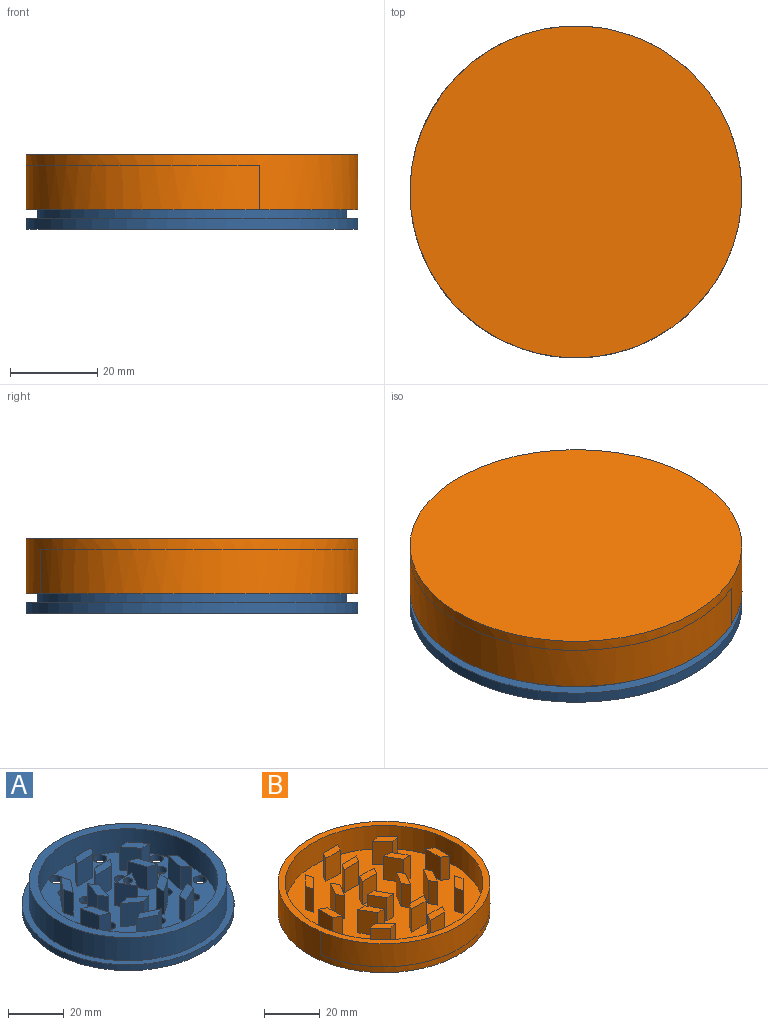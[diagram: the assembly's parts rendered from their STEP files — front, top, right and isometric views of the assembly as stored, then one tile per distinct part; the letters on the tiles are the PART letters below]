
ASSEMBLY  parts=2 mates=1
PART A: 94 faces, bbox 76.2x76.2x12.7 mm
  f0: plane 64.46x64.46mm, normal (0,0,1), area 2540.7mm2, adj f6,f7,f9,f12,f13,f14,f15,f17
  f1: cylinder r=38.1mm len=76.2mm, axis (0,0,1), area 608mm2, adj f2,f3
  f2: plane 76.2x76.2mm, normal (0,0,-1), area 4189.6mm2, adj f1,f72,f73,f74,f75,f76,f77,f78
  f3: plane 76.2x76.2mm, normal (0,0,1), area 587.8mm2, adj f1,f4
  f4: cylinder r=35.56mm len=71.12mm, axis (0,0,-1), area 2270mm2, adj f3,f5
  f5: plane 71.12x71.12mm, normal (0,0,1), area 709.6mm2, adj f4,f93
  f6: plane 10.16x8.42mm, normal (0,1,0), area 85.6mm2, adj f0,f7,f9,f10
  f7: plane 10.16x7.29mm, normal (-0.87,-0.5,0), area 85.6mm2, adj f0,f6,f9,f10
  f8: cylinder r=1.65mm len=10.16mm, axis (0,0,-1), area 105.4mm2, adj f10,f11
  f9: plane 10.16x7.29mm, normal (0.87,-0.5,0), area 85.6mm2, adj f0,f6,f7,f10
  f10: plane 8.42x7.29mm, normal (0,0,1), area 22.1mm2, adj f6,f7,f8,f9
  f11: plane 3.3x3.3mm, normal (0,0,1), area 8.6mm2, adj f8
  f12: plane 10.16x8.08mm, normal (0,-1,0), area 82.1mm2, adj f0,f13,f15,f16
  f13: plane 10.16x3.25mm, normal (0.8,-0.6,0), area 41.4mm2, adj f0,f12,f14,f16
  f14: plane 10.16x8.08mm, normal (0,1,0), area 82.1mm2, adj f0,f13,f15,f16
  f15: plane 10.16x3.25mm, normal (-0.8,0.6,0), area 41.4mm2, adj f0,f12,f14,f16
  f16: plane 10.53x3.25mm, normal (0,0,1), area 26.3mm2, adj f12,f13,f14,f15
  f17: plane 10.16x7.68mm, normal (-0.95,0.31,0), area 82.1mm2, adj f0,f18,f20,f21
  f18: plane 10.16x3.34mm, normal (-0.82,-0.57,0), area 41.4mm2, adj f0,f17,f19,f21
  f19: plane 10.16x7.68mm, normal (0.95,-0.31,0), area 82.1mm2, adj f0,f18,f20,f21
  f20: plane 10.16x3.34mm, normal (0.82,0.57,0), area 41.4mm2, adj f0,f17,f19,f21
  f21: plane 11.02x4.83mm, normal (0,0,1), area 26.3mm2, adj f17,f18,f19,f20
  f22: plane 10.16x6.53mm, normal (-0.59,-0.81,0), area 82.1mm2, adj f0,f23,f25,f26
  f23: plane 10.16x3.9mm, normal (0.29,-0.96,0), area 41.4mm2, adj f0,f22,f24,f26
  f24: plane 10.16x6.53mm, normal (0.59,0.81,0), area 82.1mm2, adj f0,f23,f25,f26
  f25: plane 10.16x3.9mm, normal (-0.29,0.96,0), area 41.4mm2, adj f0,f22,f24,f26
  f26: plane 10.43x5.94mm, normal (0,0,1), area 26.3mm2, adj f22,f23,f24,f25
  f27: plane 10.16x6.53mm, normal (0.59,-0.81,0), area 82.1mm2, adj f0,f28,f30,f31
  f28: plane 10.16x4.07mm, normal (1,-0.02,0), area 41.4mm2, adj f0,f27,f29,f31
  f29: plane 10.16x6.53mm, normal (-0.59,0.81,0), area 82.1mm2, adj f0,f28,f30,f31
  f30: plane 10.16x4.07mm, normal (-1,0.02,0), area 41.4mm2, adj f0,f27,f29,f31
  f31: plane 8.82x6.61mm, normal (0,0,1), area 26.3mm2, adj f27,f28,f29,f30
  f32: plane 10.16x7.68mm, normal (0.95,0.31,0), area 82.1mm2, adj f0,f33,f35,f36
  f33: plane 10.16x3.85mm, normal (0.33,0.95,0), area 41.4mm2, adj f0,f32,f34,f36
  f34: plane 10.16x7.68mm, normal (-0.95,-0.31,0), area 82.1mm2, adj f0,f33,f35,f36
  f35: plane 10.16x3.85mm, normal (-0.33,-0.95,0), area 41.4mm2, adj f0,f32,f34,f36
  f36: plane 9.01x6.35mm, normal (0,0,1), area 26.3mm2, adj f32,f33,f34,f35
  f37: plane 10.16x8.08mm, normal (0,-1,0), area 82.1mm2, adj f0,f38,f40,f41
  f38: plane 10.16x3.35mm, normal (0.8,-0.59,0), area 42.3mm2, adj f0,f37,f39,f41
  f39: plane 10.16x8.08mm, normal (0,1,0), area 82.1mm2, adj f0,f38,f40,f41
  f40: plane 10.16x3.35mm, normal (-0.8,0.59,0), area 42.3mm2, adj f0,f37,f39,f41
  f41: plane 10.55x3.35mm, normal (0,0,1), area 27.1mm2, adj f37,f38,f39,f40
  f42: plane 10.16x4.02mm, normal (-0.97,-0.26,0), area 42.3mm2, adj f0,f43,f45,f46
  f43: plane 10.16x6.31mm, normal (0.78,-0.62,0), area 82.1mm2, adj f0,f42,f44,f46
  f44: plane 10.16x4.02mm, normal (0.97,0.26,0), area 42.3mm2, adj f0,f43,f45,f46
  f45: plane 10.16x6.31mm, normal (-0.78,0.62,0), area 82.1mm2, adj f0,f42,f44,f46
  f46: plane 10.34x6.11mm, normal (0,0,1), area 27.1mm2, adj f42,f43,f44,f45
  f47: plane 10.16x3.82mm, normal (-0.4,-0.92,0), area 42.3mm2, adj f0,f48,f50,f51
  f48: plane 10.16x7.87mm, normal (0.97,0.22,0), area 82.1mm2, adj f0,f47,f49,f51
  f49: plane 10.16x3.82mm, normal (0.4,0.92,0), area 42.3mm2, adj f0,f48,f50,f51
  f50: plane 10.16x7.87mm, normal (-0.97,-0.22,0), area 82.1mm2, adj f0,f47,f49,f51
  f51: plane 9.54x5.61mm, normal (0,0,1), area 27.1mm2, adj f47,f48,f49,f50
  f52: plane 10.16x3.68mm, normal (0.47,-0.88,0), area 42.3mm2, adj f0,f53,f55,f56
  f53: plane 10.16x7.28mm, normal (0.43,0.9,0), area 82.1mm2, adj f0,f52,f54,f56
  f54: plane 10.16x3.68mm, normal (-0.47,0.88,0), area 42.3mm2, adj f0,f53,f55,f56
  f55: plane 10.16x7.28mm, normal (-0.43,-0.9,0), area 82.1mm2, adj f0,f52,f54,f56
  f56: plane 10.96x5.45mm, normal (0,0,1), area 27.1mm2, adj f52,f53,f54,f55
  f57: plane 10.16x4.09mm, normal (0.98,-0.19,0), area 42.3mm2, adj f0,f58,f60,f61
  f58: plane 10.16x7.28mm, normal (-0.43,0.9,0), area 82.1mm2, adj f0,f57,f59,f61
  f59: plane 10.16x4.09mm, normal (-0.98,0.19,0), area 42.3mm2, adj f0,f58,f60,f61
  f60: plane 10.16x7.28mm, normal (0.43,-0.9,0), area 82.1mm2, adj f0,f57,f59,f61
  f61: plane 8.05x7.6mm, normal (0,0,1), area 27.1mm2, adj f57,f58,f59,f60
  f62: plane 10.16x3.16mm, normal (0.76,0.65,0), area 42.3mm2, adj f0,f63,f65,f66
  f63: plane 10.16x7.87mm, normal (-0.97,0.22,0), area 82.1mm2, adj f0,f62,f64,f66
  f64: plane 10.16x3.16mm, normal (-0.76,-0.65,0), area 42.3mm2, adj f0,f63,f65,f66
  f65: plane 10.16x7.87mm, normal (0.97,-0.22,0), area 82.1mm2, adj f0,f62,f64,f66
  f66: plane 11.03x4.51mm, normal (0,0,1), area 27.1mm2, adj f62,f63,f64,f65
  f67: plane 10.16x4.16mm, normal (-0.04,1,0), area 42.3mm2, adj f0,f68,f70,f71
  f68: plane 10.16x6.31mm, normal (-0.78,-0.62,0), area 82.1mm2, adj f0,f67,f69,f71
  f69: plane 10.16x4.16mm, normal (0.04,-1,0), area 42.3mm2, adj f0,f68,f70,f71
  f70: plane 10.16x6.31mm, normal (0.78,0.62,0), area 82.1mm2, adj f0,f67,f69,f71
  f71: plane 9.2x6.47mm, normal (0,0,1), area 27.1mm2, adj f67,f68,f69,f70
  f72: cylinder r=2.44mm len=4.88mm, axis (0,0,1), area 38.9mm2, adj f0,f2
  f73: cylinder r=2.31mm len=4.62mm, axis (0,0,1), area 36.9mm2, adj f0,f2
  f74: cylinder r=2.31mm len=4.62mm, axis (0,0,1), area 36.9mm2, adj f0,f2
  f75: cylinder r=2.31mm len=4.62mm, axis (0,0,1), area 36.9mm2, adj f0,f2
  f76: cylinder r=2.31mm len=4.62mm, axis (0,0,1), area 36.9mm2, adj f0,f2
  f77: cylinder r=2.44mm len=4.88mm, axis (0,0,1), area 38.9mm2, adj f0,f2
  f78: cylinder r=2.44mm len=4.88mm, axis (0,0,1), area 38.9mm2, adj f0,f2
  f79: cylinder r=2.44mm len=4.88mm, axis (0,0,1), area 38.9mm2, adj f0,f2
  f80: cylinder r=2.44mm len=4.88mm, axis (0,0,1), area 38.9mm2, adj f0,f2
  f81: cylinder r=2.44mm len=4.88mm, axis (0,0,1), area 38.9mm2, adj f0,f2
  f82: cylinder r=2.44mm len=4.88mm, axis (0,0,1), area 38.9mm2, adj f0,f2
  f83: cylinder r=2.44mm len=4.88mm, axis (0,0,1), area 38.9mm2, adj f0,f2
  f84: cylinder r=2.44mm len=4.88mm, axis (0,0,1), area 38.9mm2, adj f0,f2
  f85: cylinder r=2.31mm len=4.62mm, axis (0,0,1), area 36.9mm2, adj f0,f2
  f86: cylinder r=2.33mm len=4.65mm, axis (0,0,1), area 37.1mm2, adj f0,f2
  f87: cylinder r=2.33mm len=4.65mm, axis (0,0,1), area 37.1mm2, adj f0,f2
  f88: cylinder r=2.33mm len=4.65mm, axis (0,0,1), area 37.1mm2, adj f0,f2
  f89: cylinder r=2.33mm len=4.65mm, axis (0,0,1), area 37.1mm2, adj f0,f2
  f90: cylinder r=2.33mm len=4.65mm, axis (0,0,1), area 37.1mm2, adj f0,f2
  f91: cylinder r=2.33mm len=4.65mm, axis (0,0,1), area 37.1mm2, adj f0,f2
  f92: cylinder r=2.33mm len=4.65mm, axis (0,0,1), area 37.1mm2, adj f0,f2
  f93: cylinder r=32.23mm len=64.46mm, axis (0,0,-1), area 2057.3mm2, adj f0,f5
PART B: 91 faces, bbox 76.2x76.2x12.7 mm
  f0: plane 71.12x71.12mm, normal (0,0,1), area 3599.7mm2, adj f4,f6,f7,f8,f9,f11,f12,f13
  f1: cylinder r=38.1mm len=76.2mm, axis (0,0,1), area 1824.1mm2, adj f2,f3,f5
  f2: plane 76.2x76.2mm, normal (0,0,-1), area 4560.4mm2, adj f1
  f3: cylinder r=38.1mm len=75.81mm, axis (0,0,-1), area 1216.1mm2, adj f1,f5
  f4: cylinder r=35.56mm len=71.12mm, axis (0,0,-1), area 2270mm2, adj f0,f5
  f5: plane 76.2x76.2mm, normal (0,0,1), area 587.7mm2, adj f1,f3,f4
  f6: plane 10.16x7.3mm, normal (0,1,0), area 74.2mm2, adj f0,f7,f9,f10
  f7: plane 10.16x3mm, normal (-0.86,0.51,0), area 35.5mm2, adj f0,f6,f8,f10
  f8: plane 10.16x7.3mm, normal (0,-1,0), area 74.2mm2, adj f0,f7,f9,f10
  f9: plane 10.16x3mm, normal (0.86,-0.51,0), area 35.5mm2, adj f0,f6,f8,f10
  f10: plane 9.08x3mm, normal (0,0,1), area 21.9mm2, adj f6,f7,f8,f9
  f11: plane 10.16x3.49mm, normal (0.01,1,0), area 35.5mm2, adj f0,f12,f14,f15
  f12: plane 10.16x6.32mm, normal (-0.87,-0.5,0), area 74.2mm2, adj f0,f11,f13,f15
  f13: plane 10.16x3.49mm, normal (-0.01,-1,0), area 35.5mm2, adj f0,f12,f14,f15
  f14: plane 10.16x6.32mm, normal (0.87,0.5,0), area 74.2mm2, adj f0,f11,f13,f15
  f15: plane 7.14x6.36mm, normal (0,0,1), area 21.9mm2, adj f11,f12,f13,f14
  f16: plane 10.16x3.04mm, normal (-0.87,-0.49,0), area 35.5mm2, adj f0,f17,f19,f20
  f17: plane 10.16x6.32mm, normal (0.87,-0.5,0), area 74.2mm2, adj f0,f16,f18,f20
  f18: plane 10.16x3.04mm, normal (0.87,0.49,0), area 35.5mm2, adj f0,f17,f19,f20
  f19: plane 10.16x6.32mm, normal (-0.87,0.5,0), area 74.2mm2, adj f0,f16,f18,f20
  f20: plane 9.36x5.36mm, normal (0,0,1), area 21.9mm2, adj f16,f17,f18,f19
  f21: plane 10.16x7.3mm, normal (0,1,0), area 74.2mm2, adj f0,f22,f24,f25
  f22: plane 10.16x3mm, normal (-0.86,0.51,0), area 35.5mm2, adj f0,f21,f23,f25
  f23: plane 10.16x7.3mm, normal (0,-1,0), area 74.2mm2, adj f0,f22,f24,f25
  f24: plane 10.16x3mm, normal (0.86,-0.51,0), area 35.5mm2, adj f0,f21,f23,f25
  f25: plane 9.08x3mm, normal (0,0,1), area 21.9mm2, adj f21,f22,f23,f24
  f26: plane 10.16x6.32mm, normal (-0.87,0.5,0), area 74.2mm2, adj f0,f27,f29,f30
  f27: plane 10.16x3.04mm, normal (-0.87,-0.49,0), area 35.5mm2, adj f0,f26,f28,f30
  f28: plane 10.16x6.32mm, normal (0.87,-0.5,0), area 74.2mm2, adj f0,f27,f29,f30
  f29: plane 10.16x3.04mm, normal (0.87,0.49,0), area 35.5mm2, adj f0,f26,f28,f30
  f30: plane 9.36x5.36mm, normal (0,0,1), area 21.9mm2, adj f26,f27,f28,f29
  f31: plane 10.16x6.32mm, normal (-0.87,-0.5,0), area 74.2mm2, adj f0,f32,f34,f35
  f32: plane 10.16x3.49mm, normal (-0.01,-1,0), area 35.5mm2, adj f0,f31,f33,f35
  f33: plane 10.16x6.32mm, normal (0.87,0.5,0), area 74.2mm2, adj f0,f32,f34,f35
  f34: plane 10.16x3.49mm, normal (0.01,1,0), area 35.5mm2, adj f0,f31,f33,f35
  f35: plane 7.14x6.36mm, normal (0,0,1), area 21.9mm2, adj f31,f32,f33,f34
  f36: plane 10.16x7.3mm, normal (0,-1,0), area 74.2mm2, adj f0,f37,f39,f40
  f37: plane 10.16x3mm, normal (0.86,-0.51,0), area 35.5mm2, adj f0,f36,f38,f40
  f38: plane 10.16x7.3mm, normal (0,1,0), area 74.2mm2, adj f0,f37,f39,f40
  f39: plane 10.16x3mm, normal (-0.86,0.51,0), area 35.5mm2, adj f0,f36,f38,f40
  f40: plane 9.08x3mm, normal (0,0,1), area 21.9mm2, adj f36,f37,f38,f39
  f41: plane 10.16x6.32mm, normal (0.87,-0.5,0), area 74.2mm2, adj f0,f42,f44,f45
  f42: plane 10.16x3.04mm, normal (0.87,0.49,0), area 35.5mm2, adj f0,f41,f43,f45
  f43: plane 10.16x6.32mm, normal (-0.87,0.5,0), area 74.2mm2, adj f0,f42,f44,f45
  f44: plane 10.16x3.04mm, normal (-0.87,-0.49,0), area 35.5mm2, adj f0,f41,f43,f45
  f45: plane 9.36x5.36mm, normal (0,0,1), area 21.9mm2, adj f41,f42,f43,f44
  f46: plane 10.16x6.32mm, normal (0.87,0.5,0), area 74.2mm2, adj f0,f47,f49,f50
  f47: plane 10.16x3.49mm, normal (0.01,1,0), area 35.5mm2, adj f0,f46,f48,f50
  f48: plane 10.16x6.32mm, normal (-0.87,-0.5,0), area 74.2mm2, adj f0,f47,f49,f50
  f49: plane 10.16x3.49mm, normal (-0.01,-1,0), area 35.5mm2, adj f0,f46,f48,f50
  f50: plane 7.14x6.36mm, normal (0,0,1), area 21.9mm2, adj f46,f47,f48,f49
  f51: plane 10.16x7.3mm, normal (0,1,0), area 74.2mm2, adj f0,f52,f54,f55
  f52: plane 10.16x3mm, normal (-0.86,0.51,0), area 35.5mm2, adj f0,f51,f53,f55
  f53: plane 10.16x7.3mm, normal (0,-1,0), area 74.2mm2, adj f0,f52,f54,f55
  f54: plane 10.16x3mm, normal (0.86,-0.51,0), area 35.5mm2, adj f0,f51,f53,f55
  f55: plane 9.08x3mm, normal (0,0,1), area 21.9mm2, adj f51,f52,f53,f54
  f56: plane 10.16x5.16mm, normal (-0.71,0.71,0), area 74.2mm2, adj f0,f57,f59,f60
  f57: plane 10.16x3.38mm, normal (-0.97,-0.25,0), area 35.5mm2, adj f0,f56,f58,f60
  f58: plane 10.16x5.16mm, normal (0.71,-0.71,0), area 74.2mm2, adj f0,f57,f59,f60
  f59: plane 10.16x3.38mm, normal (0.97,0.25,0), area 35.5mm2, adj f0,f56,f58,f60
  f60: plane 8.54x6.03mm, normal (0,0,1), area 21.9mm2, adj f56,f57,f58,f59
  f61: plane 10.16x7.3mm, normal (-1,0,0), area 74.2mm2, adj f0,f62,f64,f65
  f62: plane 10.16x3mm, normal (-0.51,-0.86,0), area 35.5mm2, adj f0,f61,f63,f65
  f63: plane 10.16x7.3mm, normal (1,0,0), area 74.2mm2, adj f0,f62,f64,f65
  f64: plane 10.16x3mm, normal (0.51,0.86,0), area 35.5mm2, adj f0,f61,f63,f65
  f65: plane 9.08x3mm, normal (0,0,1), area 21.9mm2, adj f61,f62,f63,f64
  f66: plane 10.16x5.16mm, normal (-0.71,-0.71,0), area 74.2mm2, adj f0,f67,f69,f70
  f67: plane 10.16x3.38mm, normal (0.25,-0.97,0), area 35.5mm2, adj f0,f66,f68,f70
  f68: plane 10.16x5.16mm, normal (0.71,0.71,0), area 74.2mm2, adj f0,f67,f69,f70
  f69: plane 10.16x3.38mm, normal (-0.25,0.97,0), area 35.5mm2, adj f0,f66,f68,f70
  f70: plane 8.54x6.03mm, normal (0,0,1), area 21.9mm2, adj f66,f67,f68,f69
  f71: plane 10.16x7.3mm, normal (0,-1,0), area 74.2mm2, adj f0,f72,f74,f75
  f72: plane 10.16x3mm, normal (0.86,-0.51,0), area 35.5mm2, adj f0,f71,f73,f75
  f73: plane 10.16x7.3mm, normal (0,1,0), area 74.2mm2, adj f0,f72,f74,f75
  f74: plane 10.16x3mm, normal (-0.86,0.51,0), area 35.5mm2, adj f0,f71,f73,f75
  f75: plane 9.08x3mm, normal (0,0,1), area 21.9mm2, adj f71,f72,f73,f74
  f76: plane 10.16x5.16mm, normal (0.71,-0.71,0), area 74.2mm2, adj f0,f77,f79,f80
  f77: plane 10.16x3.38mm, normal (0.97,0.25,0), area 35.5mm2, adj f0,f76,f78,f80
  f78: plane 10.16x5.16mm, normal (-0.71,0.71,0), area 74.2mm2, adj f0,f77,f79,f80
  f79: plane 10.16x3.38mm, normal (-0.97,-0.25,0), area 35.5mm2, adj f0,f76,f78,f80
  f80: plane 8.54x6.03mm, normal (0,0,1), area 21.9mm2, adj f76,f77,f78,f79
  f81: plane 10.16x7.3mm, normal (1,0,0), area 74.2mm2, adj f0,f82,f84,f85
  f82: plane 10.16x3mm, normal (0.51,0.86,0), area 35.5mm2, adj f0,f81,f83,f85
  f83: plane 10.16x7.3mm, normal (-1,0,0), area 74.2mm2, adj f0,f82,f84,f85
  f84: plane 10.16x3mm, normal (-0.51,-0.86,0), area 35.5mm2, adj f0,f81,f83,f85
  f85: plane 9.08x3mm, normal (0,0,1), area 21.9mm2, adj f81,f82,f83,f84
  f86: plane 10.16x5.16mm, normal (0.71,0.71,0), area 74.2mm2, adj f0,f87,f89,f90
  f87: plane 10.16x3.38mm, normal (-0.25,0.97,0), area 35.5mm2, adj f0,f86,f88,f90
  f88: plane 10.16x5.16mm, normal (-0.71,-0.71,0), area 74.2mm2, adj f0,f87,f89,f90
  f89: plane 10.16x3.38mm, normal (0.25,-0.97,0), area 35.5mm2, adj f0,f86,f88,f90
  f90: plane 8.54x6.03mm, normal (0,0,1), area 21.9mm2, adj f86,f87,f88,f89
PLACE A t=(-9.32,-3.85,-1.52)mm fixed
PLACE B rot(axis=(-0.48,-0.88,0),180deg) t=(-9.32,-3.86,10.55)mm
MATE cylindrical B.f3 <-> A.f1  axis (0,0,-1) through (-9.32,-3.85,10.55)mm
